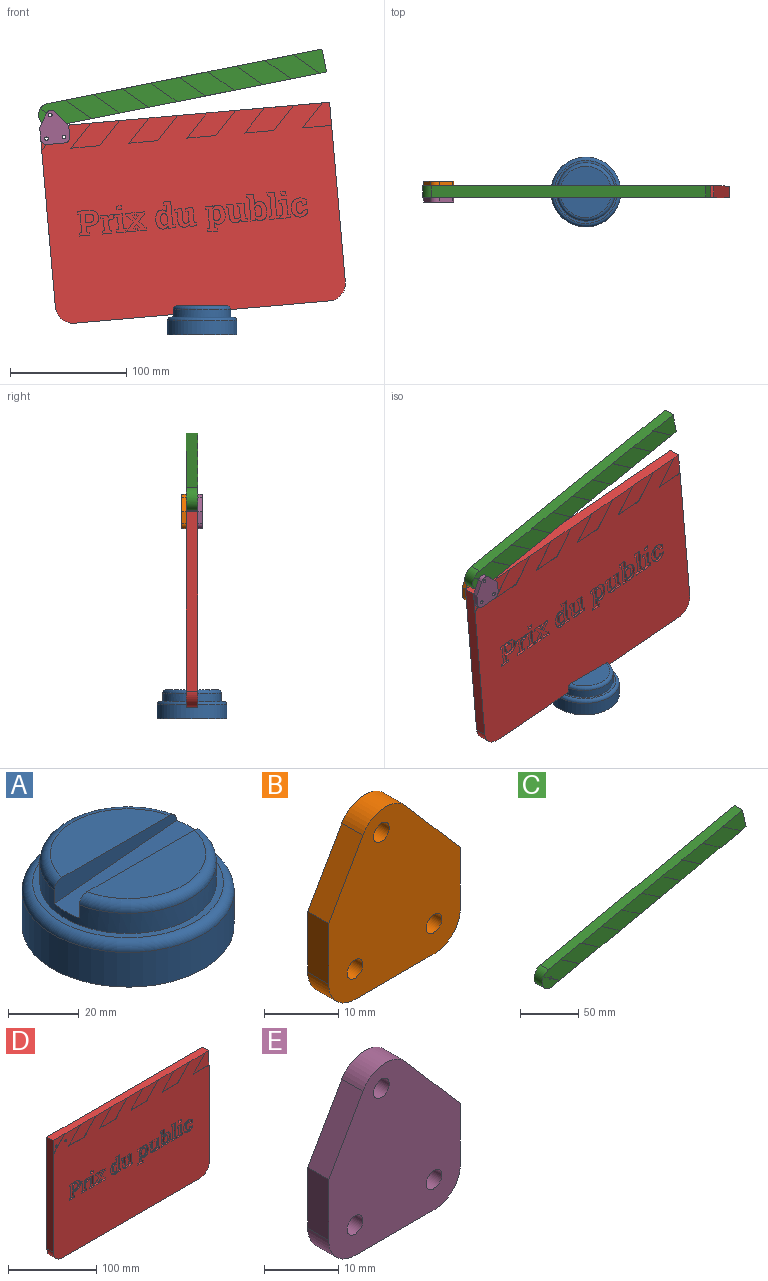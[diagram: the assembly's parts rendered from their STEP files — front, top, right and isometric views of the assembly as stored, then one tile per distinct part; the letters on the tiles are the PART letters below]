
ASSEMBLY  parts=5 mates=3
PART A: 12 faces, bbox 65x65x25 mm
  f0: plane 42.85x17mm, normal (0,0,1), area 542.2mm2, adj f1,f10
  f1: torus R=22mm, axis (0,0,1), area 306.5mm2, adj f0,f5,f10
  f2: plane 60x60mm, normal (0,0,-1), area 2827.4mm2, adj f8
  f3: plane 42.85x17mm, normal (0,0,1), area 542.2mm2, adj f4,f9
  f4: torus R=22mm, axis (0,0,1), area 306.5mm2, adj f3,f5,f9
  f5: cylinder r=25mm len=50mm, axis (0,0,1), area 1051.7mm2, adj f1,f4,f6,f9,f10,f11
  f6: plane 54x54mm, normal (0,0,1), area 326.7mm2, adj f5,f7
  f7: torus R=27mm, axis (0,0,1), area 856mm2, adj f6,f8
  f8: cylinder r=30mm len=60mm, axis (0,0,1), area 2261.9mm2, adj f2,f7
  f9: plane 48.99x7.52mm, normal (0,-1,0), area 259.4mm2, adj f3,f4,f5,f11
  f10: plane 48.99x7.52mm, normal (0,1,0), area 259.4mm2, adj f0,f1,f5,f11
  f11: plane 50.02x10.02mm, normal (-0.09,0,1), area 498.5mm2, adj f5,f9,f10
PART B: 13 faces, bbox 25x4x28.8 mm
  f0: plane 10x4mm, normal (-1,0,0), area 40mm2, adj f1,f7,f11,f12
  f1: cylinder r=5mm len=5mm, axis (0,-1,0), area 31.4mm2, adj f0,f2,f11,f12
  f2: plane 15x4mm, normal (0,0,-1), area 60mm2, adj f1,f3,f11,f12
  f3: cylinder r=5mm len=5mm, axis (0,-1,0), area 31.4mm2, adj f2,f4,f11,f12
  f4: plane 10x4mm, normal (1,0,0), area 40mm2, adj f3,f5,f11,f12
  f5: plane 12.07x10.39mm, normal (0.76,0,0.65), area 63.7mm2, adj f4,f6,f11,f12
  f6: cylinder r=5mm len=8.13mm, axis (0,-1,0), area 38.2mm2, adj f5,f7,f11,f12
  f7: plane 11.3x6.48mm, normal (-0.87,0,0.5), area 52.1mm2, adj f0,f6,f11,f12
  f8: cylinder r=1.5mm len=4mm, axis (0,-1,0), area 37.7mm2, adj f11,f12
  f9: cylinder r=1.5mm len=4mm, axis (0,-1,0), area 37.7mm2, adj f11,f12
  f10: cylinder r=1.5mm len=4mm, axis (0,-1,0), area 37.7mm2, adj f11,f12
  f11: plane 28.81x25mm, normal (0,1,0), area 549.5mm2, adj f0,f1,f2,f3,f4,f5,f6,f7
  f12: plane 28.81x25mm, normal (0,-1,0), area 549.5mm2, adj f0,f1,f2,f3,f4,f5,f6,f7
PART C: 28 faces, bbox 246.8x10x69.7 mm
  f0: plane 19.56x9.8mm, normal (0.98,0,0.21), area 196mm2, adj f1,f3,f10,f27
  f1: plane 234.76x49.9mm, normal (-0.21,0,0.98), area 2375mm2, adj f0,f2,f5,f6,f7,f8,f9,f10
  f2: cylinder r=10mm len=19.78mm, axis (0,1,0), area 309.5mm2, adj f1,f3,f9,f10,f12,f13
  f3: plane 234.76x49.9mm, normal (0.21,0,-0.98), area 2377mm2, adj f0,f2,f5,f6,f7,f8,f9,f10
  f4: cylinder r=1.5mm len=10mm, axis (0,1,0), area 93.4mm2, adj f9,f10,f11,f12,f13
  f5: plane 47.26x20.8mm, normal (0,-1,0), area 500mm2, adj f1,f3,f23,f26
  f6: plane 47.26x20.8mm, normal (0,-1,0), area 500mm2, adj f1,f3,f20,f24
  f7: plane 47.26x20.8mm, normal (0,-1,0), area 500mm2, adj f1,f3,f17,f21
  f8: plane 47.26x20.8mm, normal (0,-1,0), area 500mm2, adj f1,f3,f14,f18
  f9: plane 43.84x20.8mm, normal (0,-1,0), area 484.5mm2, adj f1,f2,f3,f4,f11,f12,f15
  f10: plane 246.83x69.68mm, normal (0,1,0), area 4950mm2, adj f0,f1,f2,f3,f4
  f11: plane 9.93x6.79mm, normal (-0.56,0,-0.83), area 2.4mm2, adj f3,f4,f9,f13
  f12: plane 7.04x4.82mm, normal (-0.56,0,-0.83), area 1.7mm2, adj f2,f4,f9,f13
  f13: plane 20.94x15.36mm, normal (0,-1,0), area 156.1mm2, adj f2,f3,f4,f11,f12
  f14: plane 22.8x15.6mm, normal (-0.56,0,-0.83), area 5.5mm2, adj f1,f3,f8,f16
  f15: plane 22.8x15.6mm, normal (0.56,0,0.83), area 5.5mm2, adj f1,f3,f9,f16
  f16: plane 47.26x20.8mm, normal (0,-1,0), area 500mm2, adj f1,f3,f14,f15
  f17: plane 22.8x15.6mm, normal (-0.56,0,-0.83), area 5.5mm2, adj f1,f3,f7,f19
  f18: plane 22.8x15.6mm, normal (0.56,0,0.83), area 5.5mm2, adj f1,f3,f8,f19
  f19: plane 47.26x20.8mm, normal (0,-1,0), area 500mm2, adj f1,f3,f17,f18
  f20: plane 22.8x15.6mm, normal (-0.56,0,-0.83), area 5.5mm2, adj f1,f3,f6,f22
  f21: plane 22.8x15.6mm, normal (0.56,0,0.83), area 5.5mm2, adj f1,f3,f7,f22
  f22: plane 47.26x20.8mm, normal (0,-1,0), area 500mm2, adj f1,f3,f20,f21
  f23: plane 22.8x15.6mm, normal (-0.56,0,-0.83), area 5.5mm2, adj f1,f3,f5,f25
  f24: plane 22.8x15.6mm, normal (0.56,0,0.83), area 5.5mm2, adj f1,f3,f6,f25
  f25: plane 47.26x20.8mm, normal (0,-1,0), area 500mm2, adj f1,f3,f23,f24
  f26: plane 22.8x15.6mm, normal (0.56,0,0.83), area 5.5mm2, adj f1,f3,f5,f27
  f27: plane 28.61x20.8mm, normal (0,-1,0), area 309.4mm2, adj f0,f1,f3,f26
PART D: 307 faces, bbox 250x10x170 mm
  f0: plane 155x10mm, normal (-1,0,0), area 1546mm2, adj f2,f3,f212,f229,f286,f287
  f1: plane 155x10mm, normal (1,0,0), area 1546mm2, adj f2,f3,f214,f229,f305,f306
  f2: plane 250x10mm, normal (0,0,1), area 2475mm2, adj f0,f1,f3,f229,f286,f287,f288,f290
  f3: plane 250x170mm, normal (0,-1,0), area 37881.8mm2, adj f0,f1,f2,f5,f6,f7,f8,f9
  f4: cylinder r=1.5mm len=9.8mm, axis (0,-1,0), area 92.4mm2, adj f229,f286
  f5: plane 10.13x2mm, normal (0,0,-1), area 20.3mm2, adj f3,f6,f228,f230
  f6: extruded ~5.76x2mm, area 12.4mm2, adj f3,f5,f7,f230
  f7: extruded ~4.92x2.11mm, area 11.1mm2, adj f3,f6,f8,f230
  f8: extruded ~4.91x2.11mm, area 11mm2, adj f3,f7,f9,f230
  f9: extruded ~5.76x2mm, area 12.4mm2, adj f3,f8,f10,f230
  f10: plane 3.6x2mm, normal (0,0,1), area 7.2mm2, adj f3,f9,f11,f230
  f11: plane 4.72x2mm, normal (-1,0,0), area 9.4mm2, adj f3,f10,f12,f230
  f12: plane 2.28x2mm, normal (-0.19,0,-0.98), area 4.6mm2, adj f3,f11,f13,f230
  f13: plane 2.56x2mm, normal (-1,0,0), area 5.1mm2, adj f3,f12,f14,f230
  f14: plane 8.81x2mm, normal (0,0,1), area 17.6mm2, adj f3,f13,f15,f230
  f15: plane 2.56x2mm, normal (1,0,0), area 5.1mm2, adj f3,f14,f16,f230
  f16: plane 2.26x2mm, normal (0.19,0,-0.98), area 4.6mm2, adj f3,f15,f17,f230
  f17: plane 15.27x2mm, normal (1,0,0), area 30.5mm2, adj f3,f16,f18,f230
  f18: plane 2.26x2mm, normal (0.19,0,0.98), area 4.6mm2, adj f3,f17,f228,f230
  f19: plane 2x2mm, normal (0.99,0,0.14), area 4mm2, adj f3,f20,f215,f279
  f20: extruded ~2x1.88mm, area 5.1mm2, adj f3,f19,f21,f279
  f21: extruded ~2.55x2mm, area 5.3mm2, adj f3,f20,f22,f279
  f22: extruded ~3.92x2mm, area 8.7mm2, adj f3,f21,f23,f279
  f23: extruded ~4.98x2mm, area 10.6mm2, adj f3,f22,f24,f279
  f24: plane 6.53x2mm, normal (1,0,0), area 13.1mm2, adj f3,f23,f25,f279
  f25: plane 2x1.74mm, normal (0.24,0,0.97), area 3.6mm2, adj f3,f24,f26,f279
  f26: plane 2.57x2mm, normal (1,0,0), area 5.1mm2, adj f3,f25,f27,f279
  f27: plane 6.01x2mm, normal (0,0,-1), area 12mm2, adj f3,f26,f28,f279
  f28: plane 9.57x2mm, normal (-1,0,0), area 19.1mm2, adj f3,f27,f29,f279
  f29: extruded ~2.47x2mm, area 5.2mm2, adj f3,f28,f30,f279
  f30: extruded ~2x1.72mm, area 3.9mm2, adj f3,f29,f31,f279
  f31: extruded ~2x1.75mm, area 3.6mm2, adj f3,f30,f32,f279
  f32: extruded ~2x1.2mm, area 3.1mm2, adj f3,f31,f33,f279
  f33: plane 8.52x2mm, normal (1,0,0), area 17mm2, adj f3,f32,f34,f279
  f34: plane 2x1.87mm, normal (0.23,0,0.97), area 3.8mm2, adj f3,f33,f35,f279
  f35: plane 2.57x2mm, normal (1,0,0), area 5.1mm2, adj f3,f34,f36,f279
  f36: plane 6.14x2mm, normal (0,0,-1), area 12.3mm2, adj f3,f35,f37,f279
  f37: plane 12.81x2mm, normal (-1,0,0), area 25.6mm2, adj f3,f36,f38,f279
  f38: plane 2x1.91mm, normal (-0.22,0,-0.97), area 3.9mm2, adj f3,f37,f39,f279
  f39: plane 2.56x2mm, normal (-1,0,0), area 5.1mm2, adj f3,f38,f215,f279
  f40: plane 2.28x2mm, normal (0.19,0,0.98), area 4.6mm2, adj f3,f41,f216,f251
  f41: plane 2.57x2mm, normal (1,0,0), area 5.1mm2, adj f3,f40,f42,f251
  f42: plane 6.2x2mm, normal (0,0,-1), area 12.4mm2, adj f3,f41,f43,f251
  f43: plane 2x1.84mm, normal (-0.99,0,-0.11), area 3.7mm2, adj f3,f42,f44,f251
  f44: extruded ~2x1.68mm, area 4.6mm2, adj f3,f43,f45,f251
  f45: extruded ~2.28x2mm, area 4.7mm2, adj f3,f44,f46,f251
  f46: extruded ~4.56x2.29mm, area 10.6mm2, adj f3,f45,f47,f251
  f47: extruded ~6.04x2mm, area 12.7mm2, adj f3,f46,f48,f251
  f48: plane 2x0.31mm, normal (-1,0,0), area 0.6mm2, adj f3,f47,f49,f251
  f49: extruded ~5.64x2mm, area 12mm2, adj f3,f48,f50,f251
  f50: extruded ~4.53x2.14mm, area 10.4mm2, adj f3,f49,f51,f251
  f51: extruded ~2.21x2mm, area 4.5mm2, adj f3,f50,f52,f251
  f52: extruded ~2x1.65mm, area 4.3mm2, adj f3,f51,f53,f251
  f53: plane 4.57x2mm, normal (-1,0,0), area 9.1mm2, adj f3,f52,f54,f251
  f54: plane 2.06x2mm, normal (-0.21,0,-0.98), area 4.2mm2, adj f3,f53,f55,f251
  f55: plane 2.57x2mm, normal (-1,0,0), area 5.1mm2, adj f3,f54,f56,f251
  f56: plane 8.38x2mm, normal (0,0,1), area 16.8mm2, adj f3,f55,f57,f251
  f57: plane 2.57x2mm, normal (1,0,0), area 5.1mm2, adj f3,f56,f58,f251
  f58: plane 2.06x2mm, normal (0.21,0,-0.98), area 4.2mm2, adj f3,f57,f216,f251
  f59: plane 2.28x2mm, normal (0.19,0,0.98), area 4.6mm2, adj f3,f60,f217,f281
  f60: plane 2.57x2mm, normal (1,0,0), area 5.1mm2, adj f3,f59,f61,f281
  f61: plane 6.55x2mm, normal (0,0,-1), area 13.1mm2, adj f3,f60,f62,f281
  f62: plane 19.8x2mm, normal (-1,0,0), area 39.6mm2, adj f3,f61,f63,f281
  f63: plane 2.06x2mm, normal (-0.21,0,-0.98), area 4.2mm2, adj f3,f62,f64,f281
  f64: plane 2.56x2mm, normal (-1,0,0), area 5.1mm2, adj f3,f63,f65,f281
  f65: plane 8.39x2mm, normal (0,0,1), area 16.8mm2, adj f3,f64,f66,f281
  f66: plane 2.56x2mm, normal (1,0,0), area 5.1mm2, adj f3,f65,f67,f281
  f67: plane 2.06x2mm, normal (0.21,0,-0.98), area 4.2mm2, adj f3,f66,f217,f281
  f68: plane 2.56x2mm, normal (1,0,0), area 5.1mm2, adj f3,f69,f218,f282
  f69: plane 2.06x2mm, normal (0.21,0,-0.98), area 4.2mm2, adj f3,f68,f70,f282
  f70: plane 9.81x2mm, normal (1,0,0), area 19.6mm2, adj f3,f69,f71,f282
  f71: plane 2.28x2mm, normal (0.19,0,0.98), area 4.6mm2, adj f3,f70,f72,f282
  f72: plane 2.57x2mm, normal (1,0,0), area 5.1mm2, adj f3,f71,f73,f282
  f73: plane 6.55x2mm, normal (0,0,-1), area 13.1mm2, adj f3,f72,f74,f282
  f74: plane 12.81x2mm, normal (-1,0,0), area 25.6mm2, adj f3,f73,f75,f282
  f75: plane 2.04x2mm, normal (-0.21,0,-0.98), area 4.2mm2, adj f3,f74,f76,f282
  f76: plane 2.56x2mm, normal (-1,0,0), area 5.1mm2, adj f3,f75,f218,f282
  f77: plane 3.2x2mm, normal (-1,0,0), area 6.4mm2, adj f3,f78,f219,f283
  f78: plane 4.27x2mm, normal (0,0,1), area 8.5mm2, adj f3,f77,f79,f283
  f79: plane 3.2x2mm, normal (1,0,0), area 6.4mm2, adj f3,f78,f219,f283
  f80: extruded ~2.41x2mm, area 5.8mm2, adj f3,f81,f220,f284
  f81: extruded ~2x1.83mm, area 4mm2, adj f3,f80,f82,f284
  f82: extruded ~2x1.78mm, area 3.9mm2, adj f3,f81,f83,f284
  f83: plane 3.86x2mm, normal (0,0,-1), area 7.7mm2, adj f3,f82,f84,f284
  f84: plane 2x0.08mm, normal (-0.89,0,-0.45), area 0.2mm2, adj f3,f83,f85,f284
  f85: extruded ~4.02x2mm, area 9.1mm2, adj f3,f84,f86,f284
  f86: extruded ~4.62x2mm, area 10mm2, adj f3,f85,f87,f284
  f87: extruded ~5.45x2.24mm, area 12.2mm2, adj f3,f86,f88,f284
  f88: extruded ~5.75x2mm, area 12.4mm2, adj f3,f87,f89,f284
  f89: plane 2x0.44mm, normal (1,0,0), area 0.9mm2, adj f3,f88,f90,f284
  f90: extruded ~5.75x2mm, area 12.4mm2, adj f3,f89,f91,f284
  f91: extruded ~5.61x2.25mm, area 12.5mm2, adj f3,f90,f92,f284
  f92: extruded ~3.44x2mm, area 7mm2, adj f3,f91,f93,f284
  f93: extruded ~2.53x2mm, area 6mm2, adj f3,f92,f94,f284
  f94: plane 4.22x2mm, normal (-1,0,-0.01), area 8.4mm2, adj f3,f93,f95,f284
  f95: plane 3.47x2mm, normal (0,0,1), area 6.9mm2, adj f3,f94,f96,f284
  f96: plane 2.47x2mm, normal (0.96,0,0.27), area 5.1mm2, adj f3,f95,f97,f284
  f97: extruded ~2x0.79mm, area 1.8mm2, adj f3,f96,f98,f284
  f98: extruded ~2x1.07mm, area 2.2mm2, adj f3,f97,f99,f284
  f99: extruded ~2.56x2mm, area 6.1mm2, adj f3,f98,f100,f284
  f100: extruded ~3.39x2mm, area 7mm2, adj f3,f99,f101,f284
  f101: plane 2x0.44mm, normal (-1,0,0), area 0.9mm2, adj f3,f100,f220,f284
  f102: plane 2x0.31mm, normal (-1,0,0), area 0.6mm2, adj f3,f103,f221,f263
  f103: extruded ~5.66x2mm, area 11.9mm2, adj f3,f102,f104,f263
  f104: extruded ~4.56x2.12mm, area 10.5mm2, adj f3,f103,f105,f263
  f105: extruded ~2.41x2mm, area 5mm2, adj f3,f104,f106,f263
  f106: extruded ~2x1.72mm, area 4.9mm2, adj f3,f105,f107,f263
  f107: plane 2x1.95mm, normal (-0.99,0,0.16), area 3.9mm2, adj f3,f106,f108,f263
  f108: plane 3.68x2mm, normal (0,0,1), area 7.4mm2, adj f3,f107,f109,f263
  f109: plane 19.79x2mm, normal (1,0,0), area 39.6mm2, adj f3,f108,f110,f263
  f110: plane 2.27x2mm, normal (0.19,0,0.98), area 4.6mm2, adj f3,f109,f111,f263
  f111: plane 2.57x2mm, normal (1,0,0), area 5.1mm2, adj f3,f110,f112,f263
  f112: plane 6.52x2mm, normal (0,0,-1), area 13mm2, adj f3,f111,f113,f263
  f113: plane 8.67x2mm, normal (-1,0,0), area 17.3mm2, adj f3,f112,f114,f263
  f114: extruded ~2x1.64mm, area 4.4mm2, adj f3,f113,f115,f263
  f115: extruded ~2.2x2mm, area 4.6mm2, adj f3,f114,f116,f263
  f116: extruded ~4.59x2.27mm, area 10.7mm2, adj f3,f115,f221,f263
  f117: plane 2x2mm, normal (0.99,0,0.14), area 4mm2, adj f3,f118,f222,f280
  f118: extruded ~2x1.88mm, area 5.1mm2, adj f3,f117,f119,f280
  f119: extruded ~2.55x2mm, area 5.3mm2, adj f3,f118,f120,f280
  f120: extruded ~3.92x2mm, area 8.7mm2, adj f3,f119,f121,f280
  f121: extruded ~4.98x2mm, area 10.6mm2, adj f3,f120,f122,f280
  f122: plane 6.53x2mm, normal (1,0,0), area 13.1mm2, adj f3,f121,f123,f280
  f123: plane 2x1.74mm, normal (0.24,0,0.97), area 3.6mm2, adj f3,f122,f124,f280
  f124: plane 2.57x2mm, normal (1,0,0), area 5.1mm2, adj f3,f123,f125,f280
  f125: plane 6.01x2mm, normal (0,0,-1), area 12mm2, adj f3,f124,f126,f280
  f126: plane 9.57x2mm, normal (-1,0,0), area 19.1mm2, adj f3,f125,f127,f280
  f127: extruded ~2.47x2mm, area 5.2mm2, adj f3,f126,f128,f280
  f128: extruded ~2x1.72mm, area 3.9mm2, adj f3,f127,f129,f280
  f129: extruded ~2x1.75mm, area 3.6mm2, adj f3,f128,f130,f280
  f130: extruded ~2x1.2mm, area 3.1mm2, adj f3,f129,f131,f280
  f131: plane 8.52x2mm, normal (1,0,0), area 17mm2, adj f3,f130,f132,f280
  f132: plane 2x1.87mm, normal (0.23,0,0.97), area 3.8mm2, adj f3,f131,f133,f280
  f133: plane 2.57x2mm, normal (1,0,0), area 5.1mm2, adj f3,f132,f134,f280
  f134: plane 6.14x2mm, normal (0,0,-1), area 12.3mm2, adj f3,f133,f135,f280
  f135: plane 12.81x2mm, normal (-1,0,0), area 25.6mm2, adj f3,f134,f136,f280
  f136: plane 2x1.91mm, normal (-0.22,0,-0.97), area 3.9mm2, adj f3,f135,f137,f280
  f137: plane 2.56x2mm, normal (-1,0,0), area 5.1mm2, adj f3,f136,f222,f280
  f138: plane 2x1.93mm, normal (0.99,0,0.16), area 3.9mm2, adj f3,f139,f223,f239
  f139: extruded ~2x1.76mm, area 4.9mm2, adj f3,f138,f140,f239
  f140: extruded ~2.32x2mm, area 4.8mm2, adj f3,f139,f141,f239
  f141: extruded ~4.54x2.14mm, area 10.4mm2, adj f3,f140,f142,f239
  f142: extruded ~5.64x2mm, area 11.9mm2, adj f3,f141,f143,f239
  f143: plane 2x0.31mm, normal (1,0,0), area 0.6mm2, adj f3,f142,f144,f239
  f144: extruded ~6.04x2mm, area 12.7mm2, adj f3,f143,f145,f239
  f145: extruded ~4.56x2.29mm, area 10.6mm2, adj f3,f144,f146,f239
  f146: extruded ~2.14x2mm, area 4.4mm2, adj f3,f145,f147,f239
  f147: extruded ~2x1.67mm, area 4.5mm2, adj f3,f146,f148,f239
  f148: plane 5.67x2mm, normal (1,0,0), area 11.3mm2, adj f3,f147,f149,f239
  f149: plane 2.28x2mm, normal (0.19,0,0.98), area 4.6mm2, adj f3,f148,f150,f239
  f150: plane 2.57x2mm, normal (1,0,0), area 5.1mm2, adj f3,f149,f151,f239
  f151: plane 6.55x2mm, normal (0,0,-1), area 13.1mm2, adj f3,f150,f152,f239
  f152: plane 19.8x2mm, normal (-1,0,0), area 39.6mm2, adj f3,f151,f153,f239
  f153: plane 2.05x2mm, normal (-0.21,0,-0.98), area 4.2mm2, adj f3,f152,f154,f239
  f154: plane 2.56x2mm, normal (-1,0,0), area 5.1mm2, adj f3,f153,f223,f239
  f155: plane 2.56x2mm, normal (1,0,0), area 5.1mm2, adj f3,f156,f224,f278
  f156: plane 2x1.48mm, normal (0.16,0,-0.99), area 3mm2, adj f3,f155,f157,f278
  f157: plane 5.2x4.29mm, normal (0.77,0,-0.64), area 13.5mm2, adj f3,f156,f158,f278
  f158: plane 5x4.15mm, normal (0.77,0,0.64), area 13mm2, adj f3,f157,f159,f278
  f159: plane 2x1.48mm, normal (0.17,0,0.99), area 3mm2, adj f3,f158,f160,f278
  f160: plane 2.57x2mm, normal (1,0,0), area 5.1mm2, adj f3,f159,f161,f278
  f161: plane 7.12x2mm, normal (0,0,-1), area 14.2mm2, adj f3,f160,f162,f278
  f162: plane 2.47x2mm, normal (-1,0,0), area 4.9mm2, adj f3,f161,f163,f278
  f163: plane 2x1.45mm, normal (-0.12,0,0.99), area 2.9mm2, adj f3,f162,f164,f278
  f164: plane 3.04x2.39mm, normal (-0.79,0,-0.62), area 7.7mm2, adj f3,f163,f165,f278
  f165: plane 3.04x2.35mm, normal (0.79,0,-0.61), area 7.7mm2, adj f3,f164,f166,f278
  f166: plane 2x1.47mm, normal (0.12,0,0.99), area 3mm2, adj f3,f165,f167,f278
  f167: plane 2.47x2mm, normal (1,0,0), area 4.9mm2, adj f3,f166,f168,f278
  f168: plane 7.15x2mm, normal (0,0,-1), area 14.3mm2, adj f3,f167,f169,f278
  f169: plane 2.57x2mm, normal (-1,0,0), area 5.1mm2, adj f3,f168,f170,f278
  f170: plane 2x1.43mm, normal (-0.17,0,0.99), area 2.9mm2, adj f3,f169,f171,f278
  f171: plane 5x4.06mm, normal (-0.78,0,0.63), area 12.9mm2, adj f3,f170,f172,f278
  f172: plane 5.2x4.28mm, normal (-0.77,0,-0.64), area 13.5mm2, adj f3,f171,f173,f278
  f173: plane 2x1.49mm, normal (-0.16,0,-0.99), area 3mm2, adj f3,f172,f174,f278
  f174: plane 2.56x2mm, normal (-1,0,0), area 5.1mm2, adj f3,f173,f175,f278
  f175: plane 7.24x2mm, normal (0,0,1), area 14.5mm2, adj f3,f174,f176,f278
  f176: plane 2.46x2mm, normal (1,0,0), area 4.9mm2, adj f3,f175,f177,f278
  f177: plane 2x1.45mm, normal (0.12,0,-0.99), area 2.9mm2, adj f3,f176,f178,f278
  f178: plane 3.19x2.46mm, normal (0.79,0,0.61), area 8mm2, adj f3,f177,f179,f278
  f179: plane 3.2x2.5mm, normal (-0.79,0,0.62), area 8.1mm2, adj f3,f178,f180,f278
  f180: plane 2x1.27mm, normal (-0.12,0,-0.99), area 2.6mm2, adj f3,f179,f181,f278
  f181: plane 2.46x2mm, normal (-1,0,0), area 4.9mm2, adj f3,f180,f224,f278
  f182: plane 3.2x2mm, normal (-1,0,0), area 6.4mm2, adj f3,f183,f225,f277
  f183: plane 4.27x2mm, normal (0,0,1), area 8.5mm2, adj f3,f182,f184,f277
  f184: plane 3.2x2mm, normal (1,0,0), area 6.4mm2, adj f3,f183,f225,f277
  f185: plane 2.56x2mm, normal (1,0,0), area 5.1mm2, adj f3,f186,f226,f276
  f186: plane 2.06x2mm, normal (0.21,0,-0.98), area 4.2mm2, adj f3,f185,f187,f276
  f187: plane 9.81x2mm, normal (1,0,0), area 19.6mm2, adj f3,f186,f188,f276
  f188: plane 2.28x2mm, normal (0.19,0,0.98), area 4.6mm2, adj f3,f187,f189,f276
  f189: plane 2.57x2mm, normal (1,0,0), area 5.1mm2, adj f3,f188,f190,f276
  f190: plane 6.55x2mm, normal (0,0,-1), area 13.1mm2, adj f3,f189,f191,f276
  f191: plane 12.81x2mm, normal (-1,0,0), area 25.6mm2, adj f3,f190,f192,f276
  f192: plane 2.04x2mm, normal (-0.21,0,-0.98), area 4.2mm2, adj f3,f191,f193,f276
  f193: plane 2.56x2mm, normal (-1,0,0), area 5.1mm2, adj f3,f192,f226,f276
  f194: plane 2.56x2mm, normal (1,0,0), area 5.1mm2, adj f3,f195,f227,f275
  f195: plane 2.04x2mm, normal (0.21,0,-0.98), area 4.2mm2, adj f3,f194,f196,f275
  f196: plane 9.81x2mm, normal (1,0,0), area 19.6mm2, adj f3,f195,f197,f275
  f197: plane 2.26x2mm, normal (0.19,0,0.98), area 4.6mm2, adj f3,f196,f198,f275
  f198: plane 2.57x2mm, normal (1,0,0), area 5.1mm2, adj f3,f197,f199,f275
  f199: plane 6.24x2mm, normal (0,0,-1), area 12.5mm2, adj f3,f198,f200,f275
  f200: plane 2.31x2mm, normal (-1,0,-0.08), area 4.6mm2, adj f3,f199,f201,f275
  f201: extruded ~2x1.91mm, area 4.8mm2, adj f3,f200,f202,f275
  f202: extruded ~2.03x2mm, area 4.4mm2, adj f3,f201,f203,f275
  f203: extruded ~2x0.71mm, area 1.4mm2, adj f3,f202,f204,f275
  f204: extruded ~2x0.62mm, area 1.3mm2, adj f3,f203,f205,f275
  f205: plane 3.89x2mm, normal (-0.99,0,0.12), area 7.8mm2, adj f3,f204,f206,f275
  f206: plane 2x1.75mm, normal (0.02,0,1), area 3.5mm2, adj f3,f205,f207,f275
  f207: extruded ~2x1.55mm, area 3.2mm2, adj f3,f206,f208,f275
  f208: extruded ~2x1.04mm, area 2.8mm2, adj f3,f207,f209,f275
  f209: plane 7.68x2mm, normal (-1,0,0), area 15.4mm2, adj f3,f208,f210,f275
  f210: plane 2.04x2mm, normal (-0.21,0,-0.98), area 4.2mm2, adj f3,f209,f211,f275
  f211: plane 2.56x2mm, normal (-1,0,0), area 5.1mm2, adj f3,f210,f227,f275
  f212: cylinder r=15mm len=15mm, axis (0,1,0), area 235.6mm2, adj f0,f3,f213,f229
  f213: plane 220x10mm, normal (0,0,-1), area 2200mm2, adj f3,f212,f214,f229
  f214: cylinder r=15mm len=15mm, axis (0,1,0), area 235.6mm2, adj f1,f3,f213,f229
  f215: plane 5.65x2mm, normal (0,0,1), area 11.3mm2, adj f3,f19,f39,f279
  f216: plane 15.87x2mm, normal (1,0,0), area 31.7mm2, adj f3,f40,f58,f251
  f217: plane 16.79x2mm, normal (1,0,0), area 33.6mm2, adj f3,f59,f67,f281
  f218: plane 8.37x2mm, normal (0,0,1), area 16.7mm2, adj f3,f68,f76,f282
  f219: plane 4.27x2mm, normal (0,0,-1), area 8.5mm2, adj f3,f77,f79,f283
  f220: extruded ~3.41x2mm, area 7mm2, adj f3,f80,f101,f284
  f221: extruded ~6.06x2mm, area 12.7mm2, adj f3,f102,f116,f263
  f222: plane 5.65x2mm, normal (0,0,1), area 11.3mm2, adj f3,f117,f137,f280
  f223: plane 5.74x2mm, normal (0,0,1), area 11.5mm2, adj f3,f138,f154,f239
  f224: plane 7.04x2mm, normal (0,0,1), area 14.1mm2, adj f3,f155,f181,f278
  f225: plane 4.27x2mm, normal (0,0,-1), area 8.5mm2, adj f3,f182,f184,f277
  f226: plane 8.37x2mm, normal (0,0,1), area 16.7mm2, adj f3,f185,f193,f276
  f227: plane 8.36x2mm, normal (0,0,1), area 16.7mm2, adj f3,f194,f211,f275
  f228: plane 2.57x2mm, normal (1,0,0), area 5.1mm2, adj f3,f5,f18,f230
  f229: plane 250x170mm, normal (0,1,0), area 42389.3mm2, adj f0,f1,f2,f4,f212,f213,f214,f285
  f230: plane 21.28x18.01mm, normal (0,-1,0), area 199.5mm2, adj f5,f6,f7,f8,f9,f10,f11,f12
  f231: plane 7.21x6.99mm, normal (0,-1,0), area 45.7mm2, adj f232,f233,f234,f235,f236,f237,f238
  f232: plane 3.6x2mm, normal (0,0,1), area 7.2mm2, adj f230,f231,f233,f238
  f233: extruded ~2.7x2mm, area 5.9mm2, adj f230,f231,f232,f234
  f234: extruded ~2.53x2mm, area 5.5mm2, adj f230,f231,f233,f235
  f235: extruded ~2.48x2mm, area 5.4mm2, adj f230,f231,f234,f236
  f236: extruded ~2.7x2mm, area 5.9mm2, adj f230,f231,f235,f237
  f237: plane 3.6x2mm, normal (0,0,-1), area 7.2mm2, adj f230,f231,f236,f238
  f238: plane 6.99x2mm, normal (-1,0,0), area 14mm2, adj f230,f231,f232,f237
  f239: plane 23.11x16.3mm, normal (0,-1,0), area 200.9mm2, adj f138,f139,f140,f141,f142,f143,f144,f145
  f240: plane 9.77x5.72mm, normal (0,-1,0), area 48.7mm2, adj f241,f242,f243,f244,f245,f246,f247,f248
  f241: extruded ~3.62x2mm, area 7.5mm2, adj f239,f240,f242,f250
  f242: extruded ~2.28x2mm, area 5.7mm2, adj f239,f240,f241,f243
  f243: extruded ~2x1.6mm, area 3.3mm2, adj f239,f240,f242,f244
  f244: extruded ~2x1.17mm, area 3.3mm2, adj f239,f240,f243,f245
  f245: plane 6.71x2mm, normal (1,0,0), area 13.4mm2, adj f239,f240,f244,f246
  f246: extruded ~2x1.13mm, area 3.2mm2, adj f239,f240,f245,f247
  f247: extruded ~2x1.62mm, area 3.4mm2, adj f239,f240,f246,f248
  f248: extruded ~2.27x2mm, area 5.4mm2, adj f239,f240,f247,f249
  f249: extruded ~3.27x2mm, area 6.8mm2, adj f239,f240,f248,f250
  f250: plane 2x0.31mm, normal (-1,0,0), area 0.6mm2, adj f239,f240,f241,f249
  f251: plane 22.19x16.55mm, normal (0,-1,0), area 202.9mm2, adj f40,f41,f42,f43,f44,f45,f46,f47
  f252: plane 9.82x5.74mm, normal (0,-1,0), area 49.3mm2, adj f253,f254,f255,f256,f257,f258,f259,f260
  f253: extruded ~3.29x2mm, area 6.8mm2, adj f251,f252,f254,f262
  f254: extruded ~2.27x2mm, area 5.4mm2, adj f251,f252,f253,f255
  f255: extruded ~2x1.68mm, area 3.5mm2, adj f251,f252,f254,f256
  f256: extruded ~2x1.07mm, area 3mm2, adj f251,f252,f255,f257
  f257: plane 6.93x2mm, normal (-1,0,0), area 13.9mm2, adj f251,f252,f256,f258
  f258: extruded ~2x1.13mm, area 3.2mm2, adj f251,f252,f257,f259
  f259: extruded ~2x1.64mm, area 3.4mm2, adj f251,f252,f258,f260
  f260: extruded ~2.28x2mm, area 5.6mm2, adj f251,f252,f259,f261
  f261: extruded ~3.62x2mm, area 7.5mm2, adj f251,f252,f260,f262
  f262: plane 2x0.31mm, normal (1,0,0), area 0.6mm2, adj f251,f252,f253,f261
  f263: plane 23.11x16.53mm, normal (0,-1,0), area 195.1mm2, adj f102,f103,f104,f105,f106,f107,f108,f109
  f264: plane 9.77x5.76mm, normal (0,-1,0), area 49.5mm2, adj f265,f266,f267,f268,f269,f270,f271,f272
  f265: extruded ~3.29x2mm, area 6.8mm2, adj f263,f264,f266,f274
  f266: extruded ~2.31x2mm, area 5.4mm2, adj f263,f264,f265,f267
  f267: extruded ~2x1.7mm, area 3.5mm2, adj f263,f264,f266,f268
  f268: extruded ~2x1.11mm, area 3.2mm2, adj f263,f264,f267,f269
  f269: plane 6.68x2mm, normal (-1,0,0), area 13.4mm2, adj f263,f264,f268,f270
  f270: extruded ~2x1.19mm, area 3.3mm2, adj f263,f264,f269,f271
  f271: extruded ~2x1.68mm, area 3.5mm2, adj f263,f264,f270,f272
  f272: extruded ~2.32x2mm, area 5.7mm2, adj f263,f264,f271,f273
  f273: extruded ~3.66x2mm, area 7.5mm2, adj f263,f264,f272,f274
  f274: plane 2x0.31mm, normal (1,0,0), area 0.6mm2, adj f263,f264,f265,f273
  f275: plane 16.11x11.22mm, normal (0,-1,0), area 101.3mm2, adj f194,f195,f196,f197,f198,f199,f200,f201
  f276: plane 15.81x8.59mm, normal (0,-1,0), area 85.3mm2, adj f185,f186,f187,f188,f189,f190,f191,f192
  f277: plane 4.27x3.2mm, normal (0,-1,0), area 13.7mm2, adj f182,f183,f184,f225
  f278: plane 16.51x15.81mm, normal (0,-1,0), area 158mm2, adj f155,f156,f157,f158,f159,f160,f161,f162
  f279: plane 17.44x16.12mm, normal (0,-1,0), area 162.2mm2, adj f19,f20,f21,f22,f23,f24,f25,f26
  f280: plane 17.44x16.12mm, normal (0,-1,0), area 162.2mm2, adj f117,f118,f119,f120,f121,f122,f123,f124
  f281: plane 22.8x8.61mm, normal (0,-1,0), area 115.1mm2, adj f59,f60,f61,f62,f63,f64,f65,f66
  f282: plane 15.81x8.59mm, normal (0,-1,0), area 85.3mm2, adj f68,f69,f70,f71,f72,f73,f74,f75
  f283: plane 4.27x3.2mm, normal (0,-1,0), area 13.7mm2, adj f77,f78,f79,f219
  f284: plane 16.42x13.84mm, normal (0,-1,0), area 126.4mm2, adj f80,f81,f82,f83,f84,f85,f86,f87
  f285: cylinder r=1.5mm len=10mm, axis (0,-1,0), area 94.2mm2, adj f3,f229
  f286: plane 20x19.06mm, normal (0,-1,0), area 183.6mm2, adj f0,f2,f4,f287
  f287: plane 20x19.06mm, normal (-0.72,0,0.69), area 5.5mm2, adj f0,f2,f3,f286
  f288: plane 20x19.06mm, normal (0.72,0,-0.69), area 5.5mm2, adj f2,f3,f289,f291
  f289: plane 25x0.2mm, normal (0,0,1), area 5mm2, adj f3,f288,f290,f291
  f290: plane 20x19.06mm, normal (-0.72,0,0.69), area 5.5mm2, adj f2,f3,f289,f291
  f291: plane 44.06x20mm, normal (0,-1,0), area 500mm2, adj f2,f288,f289,f290
  f292: plane 20x19.06mm, normal (0.72,0,-0.69), area 5.5mm2, adj f2,f3,f293,f295
  f293: plane 25x0.2mm, normal (0,0,1), area 5mm2, adj f3,f292,f294,f295
  f294: plane 20x19.06mm, normal (-0.72,0,0.69), area 5.5mm2, adj f2,f3,f293,f295
  f295: plane 44.06x20mm, normal (0,-1,0), area 500mm2, adj f2,f292,f293,f294
  f296: plane 20x19.06mm, normal (0.72,0,-0.69), area 5.5mm2, adj f2,f3,f297,f299
  f297: plane 25x0.2mm, normal (0,0,1), area 5mm2, adj f3,f296,f298,f299
  f298: plane 20x19.06mm, normal (-0.72,0,0.69), area 5.5mm2, adj f2,f3,f297,f299
  f299: plane 44.06x20mm, normal (0,-1,0), area 500mm2, adj f2,f296,f297,f298
  f300: plane 20x19.06mm, normal (0.72,0,-0.69), area 5.5mm2, adj f2,f3,f301,f303
  f301: plane 25x0.2mm, normal (0,0,1), area 5mm2, adj f3,f300,f302,f303
  f302: plane 20x19.06mm, normal (-0.72,0,0.69), area 5.5mm2, adj f2,f3,f301,f303
  f303: plane 44.06x20mm, normal (0,-1,0), area 500mm2, adj f2,f300,f301,f302
  f304: plane 20x19.06mm, normal (0.72,0,-0.69), area 5.5mm2, adj f2,f3,f305,f306
  f305: plane 25x0.2mm, normal (0,0,1), area 5mm2, adj f1,f3,f304,f306
  f306: plane 25x20mm, normal (0,-1,0), area 309.4mm2, adj f1,f2,f304,f305
PART E: 13 faces, bbox 25x4x28.8 mm
  f0: plane 10x4mm, normal (-1,0,0), area 40mm2, adj f1,f7,f11,f12
  f1: cylinder r=5mm len=5mm, axis (0,1,0), area 31.4mm2, adj f0,f2,f11,f12
  f2: plane 15x4mm, normal (0,0,-1), area 60mm2, adj f1,f3,f11,f12
  f3: cylinder r=5mm len=5mm, axis (0,1,0), area 31.4mm2, adj f2,f4,f11,f12
  f4: plane 10x4mm, normal (1,0,0), area 40mm2, adj f3,f5,f11,f12
  f5: plane 12.07x10.39mm, normal (0.76,0,0.65), area 63.7mm2, adj f4,f6,f11,f12
  f6: cylinder r=5mm len=8.13mm, axis (0,1,0), area 38.2mm2, adj f5,f7,f11,f12
  f7: plane 11.3x6.48mm, normal (-0.87,0,0.5), area 52.1mm2, adj f0,f6,f11,f12
  f8: cylinder r=1.5mm len=4mm, axis (0,1,0), area 37.7mm2, adj f11,f12
  f9: cylinder r=1.5mm len=4mm, axis (0,1,0), area 37.7mm2, adj f11,f12
  f10: cylinder r=1.5mm len=4mm, axis (0,1,0), area 37.7mm2, adj f11,f12
  f11: plane 28.81x25mm, normal (0,-1,0), area 549.5mm2, adj f0,f1,f2,f3,f4,f5,f6,f7
  f12: plane 28.81x25mm, normal (0,1,0), area 549.5mm2, adj f0,f1,f2,f3,f4,f5,f6,f7
PLACE A t=(-87.92,-34.45,-69.9)mm
PLACE B rot(axis=(0,-1,0),5deg) t=(-95.33,-29.45,34.4)mm
PLACE C rot(axis=(0,1,0),0.8deg) t=(-104.44,-29.45,22.51)mm
PLACE D rot(axis=(0,-1,0),5deg) t=(-95.33,-29.45,34.4)mm fixed
PLACE E rot(axis=(0,-1,0),5deg) t=(-95.33,-29.45,34.4)mm
MATE fastened A.f11 <-> D.f213  axis (-0.09,0,1) through (-87.92,-34.45,-50.27)mm
MATE revolute C.f2 <-> E.f10  axis (0,-1,0) through (-218.17,-39.45,119.02)mm
MATE fastened B.f1 <-> D.f4  axis (0,-1,0) through (-221.41,-29.45,98.66)mm
